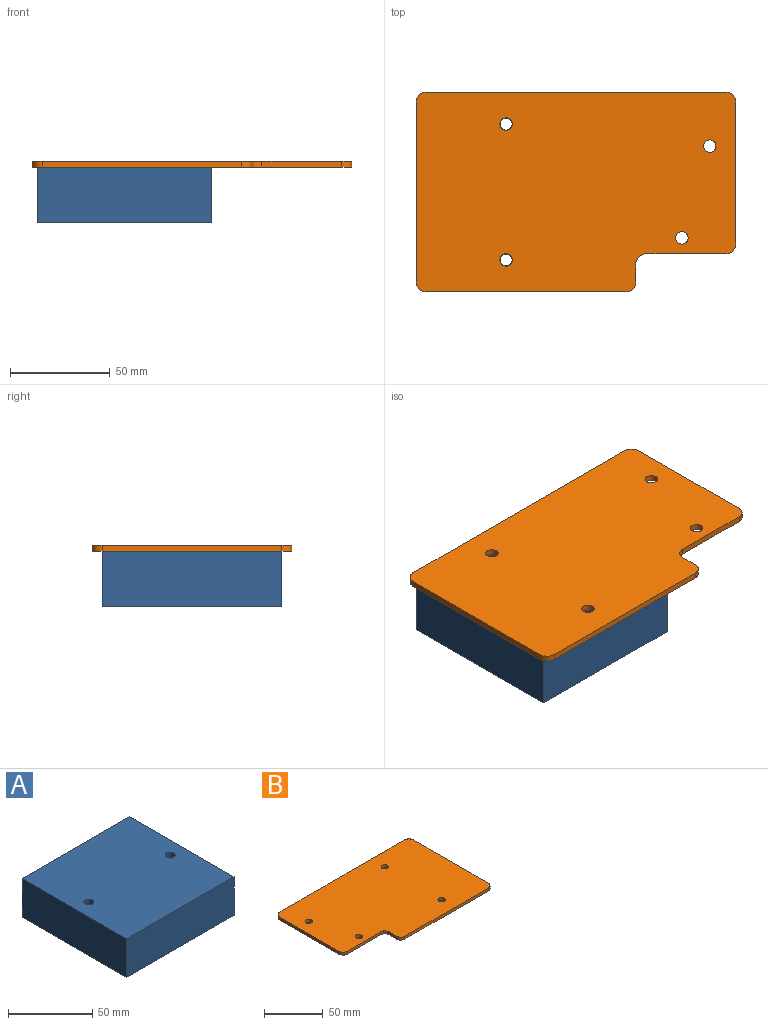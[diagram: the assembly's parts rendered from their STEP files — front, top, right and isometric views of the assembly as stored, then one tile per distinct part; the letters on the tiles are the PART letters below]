
ASSEMBLY  parts=2 mates=2
PART A: 8 faces, bbox 90x87.5x28 mm
  f0: plane 90x28mm, normal (0,-1,0), area 2520mm2, adj f1,f3,f6,f7
  f1: plane 87.5x28mm, normal (1,0,0), area 2450mm2, adj f0,f2,f6,f7
  f2: plane 90x28mm, normal (0,1,0), area 2520mm2, adj f1,f3,f6,f7
  f3: plane 87.5x28mm, normal (-1,0,0), area 2450mm2, adj f0,f2,f6,f7
  f4: cylinder r=3mm len=28mm, axis (0,0,-1), area 527.8mm2, adj f6,f7
  f5: cylinder r=3mm len=28mm, axis (0,0,-1), area 527.8mm2, adj f6,f7
  f6: plane 90x87.5mm, normal (0,0,1), area 7818.5mm2, adj f0,f1,f2,f3,f4,f5
  f7: plane 90x87.5mm, normal (0,0,-1), area 7818.5mm2, adj f0,f1,f2,f3,f4,f5
PART B: 18 faces, bbox 160x100x3 mm
  f0: plane 100x3mm, normal (0,-1,0), area 300mm2, adj f10,f11,f12,f17
  f1: plane 90x3mm, normal (1,0,0), area 270mm2, adj f10,f11,f12,f13
  f2: plane 150x3mm, normal (0,1,0), area 450mm2, adj f10,f11,f13,f14
  f3: plane 71x3mm, normal (-1,0,0), area 213mm2, adj f10,f11,f14,f15
  f4: plane 40x3mm, normal (0,-1,0), area 120mm2, adj f10,f11,f15,f16
  f5: cylinder r=3.1mm len=6.2mm, axis (0,0,-1), area 58.4mm2, adj f10,f11
  f6: cylinder r=3.1mm len=6.2mm, axis (0,0,-1), area 58.4mm2, adj f10,f11
  f7: cylinder r=3.1mm len=6.2mm, axis (0,0,-1), area 58.4mm2, adj f10,f11
  f8: cylinder r=3.1mm len=6.2mm, axis (0,0,-1), area 58.4mm2, adj f10,f11
  f9: plane 9x3mm, normal (-1,0,0), area 27mm2, adj f10,f11,f16,f17
  f10: plane 160x100mm, normal (0,0,1), area 14907.8mm2, adj f0,f1,f2,f3,f4,f5,f6,f7
  f11: plane 160x100mm, normal (0,0,-1), area 14907.8mm2, adj f0,f1,f2,f3,f4,f5,f6,f7
  f12: cylinder r=5mm len=5mm, axis (0,0,1), area 23.6mm2, adj f0,f1,f10,f11
  f13: cylinder r=5mm len=5mm, axis (0,0,-1), area 23.6mm2, adj f1,f2,f10,f11
  f14: cylinder r=5mm len=5mm, axis (0,0,1), area 23.6mm2, adj f2,f3,f10,f11
  f15: cylinder r=5mm len=5mm, axis (0,0,1), area 23.6mm2, adj f3,f4,f10,f11
  f16: cylinder r=5mm len=5mm, axis (0,0,-1), area 23.6mm2, adj f4,f9,f10,f11
  f17: cylinder r=5mm len=5mm, axis (0,0,-1), area 23.6mm2, adj f0,f9,f10,f11
PLACE A rot(axis=(0,0,-1),90deg) t=(-115.98,-191.58,81.98)mm
PLACE B rot(axis=(0,1,0),180deg) t=(-10.63,-172.91,112.98)mm
MATE pin_slot A.f5 <-> B.f7  axis (0,0,1) through (-74.91,-112.59,109.98)mm
MATE parallel A.f7 <-> B.f11  axis (0,0,-1) through (-73.65,-146.59,81.98)mm
